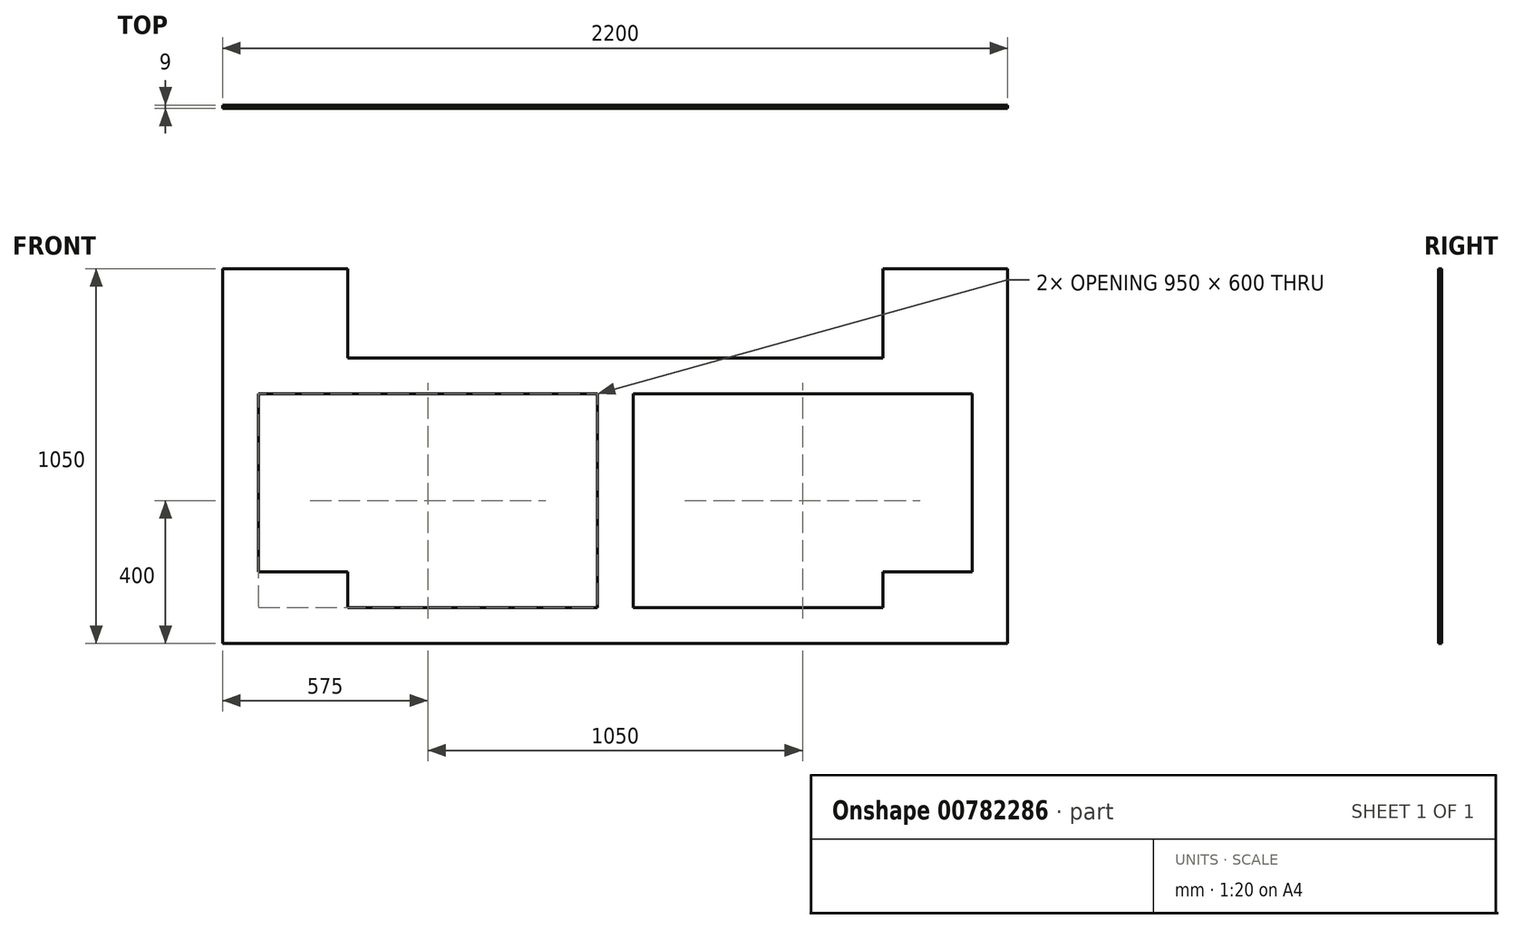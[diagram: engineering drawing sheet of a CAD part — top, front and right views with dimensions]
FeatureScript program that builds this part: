
annotation { "Feature Type Name" : "Feature", "Feature Type Description" : "" }
export const myFeature = defineFeature(function(context is Context, id is Id, definition is map)
    precondition{}
    {
        {
            var Q0;
            Q0=qCreatedBy(makeId("Front.planeOp"),FACE);
            var sketch = newSketch(context, id + "F0", { "sketchPlane" : qUnion([Q0])});
            skLineSegment(sketch, "E0", {"start": v(0, 0) * mm, "end": v(2200, 0) * mm});
            skLineSegment(sketch, "E1", {"start": v(2200, 0) * mm, "end": v(2200, 1050) * mm});
            skLineSegment(sketch, "E2", {"start": v(2200, 1050) * mm, "end": v(1850, 1050) * mm});
            skLineSegment(sketch, "E3", {"start": v(1850, 1050) * mm, "end": v(1850, 800) * mm});
            skLineSegment(sketch, "E4", {"start": v(1850, 800) * mm, "end": v(350, 800) * mm});
            skLineSegment(sketch, "E5", {"start": v(350, 800) * mm, "end": v(350, 1050) * mm});
            skLineSegment(sketch, "E6", {"start": v(350, 1050) * mm, "end": v(0, 1050) * mm});
            skLineSegment(sketch, "E7", {"start": v(0, 1050) * mm, "end": v(0, 0) * mm});
            skLineSegment(sketch, "E8", {"start": v(100, 700) * mm, "end": v(100, 200) * mm});
            skLineSegment(sketch, "E9", {"start": v(100, 200) * mm, "end": v(350, 200) * mm});
            skLineSegment(sketch, "E10", {"start": v(350, 200) * mm, "end": v(350, 100) * mm});
            skLineSegment(sketch, "E11", {"start": v(350, 100) * mm, "end": v(1050, 100) * mm});
            skLineSegment(sketch, "E12", {"start": v(1050, 100) * mm, "end": v(1050, 700) * mm});
            skLineSegment(sketch, "E13", {"start": v(1050, 700) * mm, "end": v(100, 700) * mm});
            skLineSegment(sketch, "E14", {"start": v(1150, 100) * mm, "end": v(1150, 700) * mm});
            skLineSegment(sketch, "E15", {"start": v(1150, 700) * mm, "end": v(2100, 700) * mm});
            skLineSegment(sketch, "E16", {"start": v(2100, 700) * mm, "end": v(2100, 200) * mm});
            skLineSegment(sketch, "E17", {"start": v(2100, 200) * mm, "end": v(1850, 200) * mm});
            skLineSegment(sketch, "E18", {"start": v(1850, 200) * mm, "end": v(1850, 100) * mm});
            skLineSegment(sketch, "E19", {"start": v(1850, 100) * mm, "end": v(1150, 100) * mm});
            skLineSegment(sketch, "E20", {"start": v(1100, 800) * mm, "end": v(1100, 0) * mm, "construction": true});
            skLineSegment(sketch, "E21", {"start": v(1050, 400) * mm, "end": v(1150, 400) * mm, "construction": true});
            skSolve(sketch);
        }
        {
            var Q0;
            Q0 = qSketchRegion(id + "F0", true);
            extrude(context, id + "F1", {"entities" : qUnion([Q0]), "depth" : 9 * mm, "offsetDistance" : 25 * mm});
        }
    });
